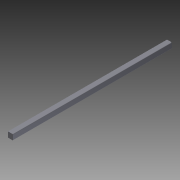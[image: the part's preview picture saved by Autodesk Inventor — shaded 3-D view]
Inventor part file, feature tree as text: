
AUTODESK INVENTOR PART (.ipt)
format: ipt  version: 2014 (Build 180170000, 170)  size: 182,272 bytes
history: native  units: in
note: dims shown in document units (in); Inventor stores cm internally (conversion verified against a paired STEP export)
features: projected_geometry x8, extrude x3, sketch x3, other x1, imported_body x1
ambient origin geometry x8: Origin, YZ Plane, XZ Plane, XY Plane, X Axis, Y Axis, Z Axis, Center Point
bodies: Body1 (feature_tree)
feature tree (16):
  parser-record x1  (decoder bookkeeping rows leaked as tree rows — omitted from the tree; the rows remain in map.json)
  imported_body  "Base1"
  extrude  "Extrusion1"  Depth=0.5in TaperAngle=0.0deg
  extrude  "Extrusion2"  Depth=1.0in TaperAngle=0.0deg
  extrude  "Extrusion3"  [1 undecoded]
  sketch  "Sketch1"  dims[d0=6.5in d1=0.0in d2=0.5in d3=0.0in]
  projected_geometry  "Projected Loop1"
  projected_geometry  "Projected Loop2"
  projected_geometry  "Projected Loop3"
  projected_geometry  "Projected Loop4"
  projected_geometry  "Projected Loop5"
  projected_geometry  "Projected Loop6"
  projected_geometry  "Projected Loop7"
  projected_geometry  "Projected Loop8"
  sketch  "Sketch2"  dims[d4=3.7in d5=1.0in d6=0.0in]
  sketch  "Sketch3"
note: 1 required parameter value undecoded (feature->parameter linkage not recoverable at this tier; creation-order binding heuristic only, values carry confidence <= 0.55)
